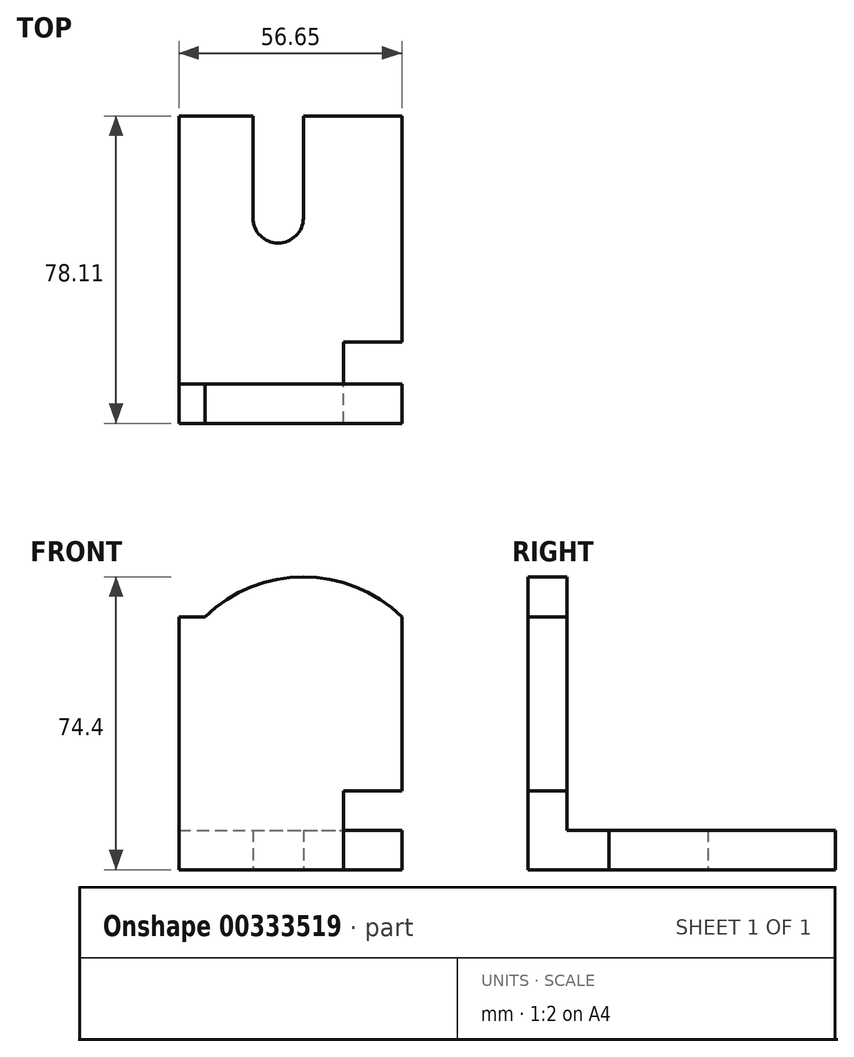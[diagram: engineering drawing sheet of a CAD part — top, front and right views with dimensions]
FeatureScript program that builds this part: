
annotation { "Feature Type Name" : "Feature", "Feature Type Description" : "" }
export const myFeature = defineFeature(function(context is Context, id is Id, definition is map)
    precondition{}
    {
        {
            var Q0;
            Q0=qCreatedBy(makeId("Top.planeOp"),FACE);
            var sketch = newSketch(context, id + "F0", { "sketchPlane" : qUnion([Q0])});
            skLineSegment(sketch, "E0.bottom", {"start": v(-31.63, 0) * mm, "end": v(25.02, 0) * mm});
            skLineSegment(sketch, "E0.top", {"start": v(-31.63, 78.11) * mm, "end": v(-12.83, 78.11) * mm});
            skLineSegment(sketch, "E0.left", {"start": v(-31.63, 0) * mm, "end": v(-31.63, 78.11) * mm});
            skLineSegment(sketch, "E0.right", {"start": v(25.02, 0) * mm, "end": v(25.02, 78.11) * mm});
            skLineSegment(sketch, "E1.left", {"start": v(-12.83, 78.11) * mm, "end": v(-12.83, 52.2) * mm});
            skLineSegment(sketch, "E1.right", {"start": v(0, 78.11) * mm, "end": v(0, 52.2) * mm});
            skArc(sketch, "E2", {"start": v(0, 52.2) * mm, "mid": v(-6.41, 45.79) * mm, "end": v(-12.83, 52.2) * mm});
            skLineSegment(sketch, "E3.trimOffspring", {"start": v(0, 78.11) * mm, "end": v(25.02, 78.11) * mm});
            skLineSegment(sketch, "E4.bottom", {"start": v(25.02, 0) * mm, "end": v(13.08, 0) * mm});
            skLineSegment(sketch, "E4.top", {"start": v(25.02, 19.94) * mm, "end": v(13.08, 19.94) * mm});
            skLineSegment(sketch, "E4.left", {"start": v(25.02, 0) * mm, "end": v(25.02, 19.94) * mm});
            skLineSegment(sketch, "E4.right", {"start": v(13.08, 0) * mm, "end": v(13.08, 19.94) * mm});
            skSolve(sketch);
        }
        {
            var Q0;
            Q0 = qSketchRegion(id + "F0", true);
            extrude(context, id + "F1", {"entities" : qUnion([Q0]), "depth" : 10 * mm, "offsetDistance" : 25 * mm});
        }
        {
            var Q0;
            Q0=qCreatedBy(makeId("Front.planeOp"),FACE);
            var sketch = newSketch(context, id + "F2", { "sketchPlane" : qUnion([Q0])});
            skLineSegment(sketch, "E5.bottom", {"start": v(25.02, 0) * mm, "end": v(-31.63, 0) * mm});
            skLineSegment(sketch, "E5.top", {"start": v(25.02, 64.14) * mm, "end": v(-31.63, 64.14) * mm});
            skLineSegment(sketch, "E5.left", {"start": v(25.02, 0) * mm, "end": v(25.02, 64.14) * mm});
            skLineSegment(sketch, "E5.right", {"start": v(-31.63, 0) * mm, "end": v(-31.63, 64.14) * mm});
            skArc(sketch, "E6", {"start": v(25.02, 64.14) * mm, "mid": v(0, 74.4) * mm, "end": v(-25.02, 64.14) * mm});
            skSolve(sketch);
        }
        {
            var Q0;
            Q0 = qSketchRegion(id + "F2", true);
            extrude(context, id + "F3", {"entities" : qUnion([Q0]), "operationType" : NewBodyOperationType.ADD, "oppositeDirection" : true, "depth" : 10 * mm, "offsetDistance" : 25 * mm});
        }
        {
            var Q0;
            Q0=qCreatedBy(makeId("Top.planeOp"),FACE);
            var sketch = newSketch(context, id + "F4", { "sketchPlane" : qUnion([Q0])});
            skLineSegment(sketch, "E7.bottom", {"start": v(25.02, 0) * mm, "end": v(10.24, 0) * mm});
            skLineSegment(sketch, "E7.top", {"start": v(25.02, 20.62) * mm, "end": v(10.24, 20.62) * mm});
            skLineSegment(sketch, "E7.left", {"start": v(25.02, 0) * mm, "end": v(25.02, 20.62) * mm});
            skLineSegment(sketch, "E7.right", {"start": v(10.24, 0) * mm, "end": v(10.24, 20.62) * mm});
            skSolve(sketch);
        }
        {
            var Q0;
            Q0 = qSketchRegion(id + "F4", true);
            extrude(context, id + "F5", {"entities" : qUnion([Q0]), "operationType" : NewBodyOperationType.REMOVE, "depth" : 20 * mm, "offsetDistance" : 25 * mm});
        }
    });
